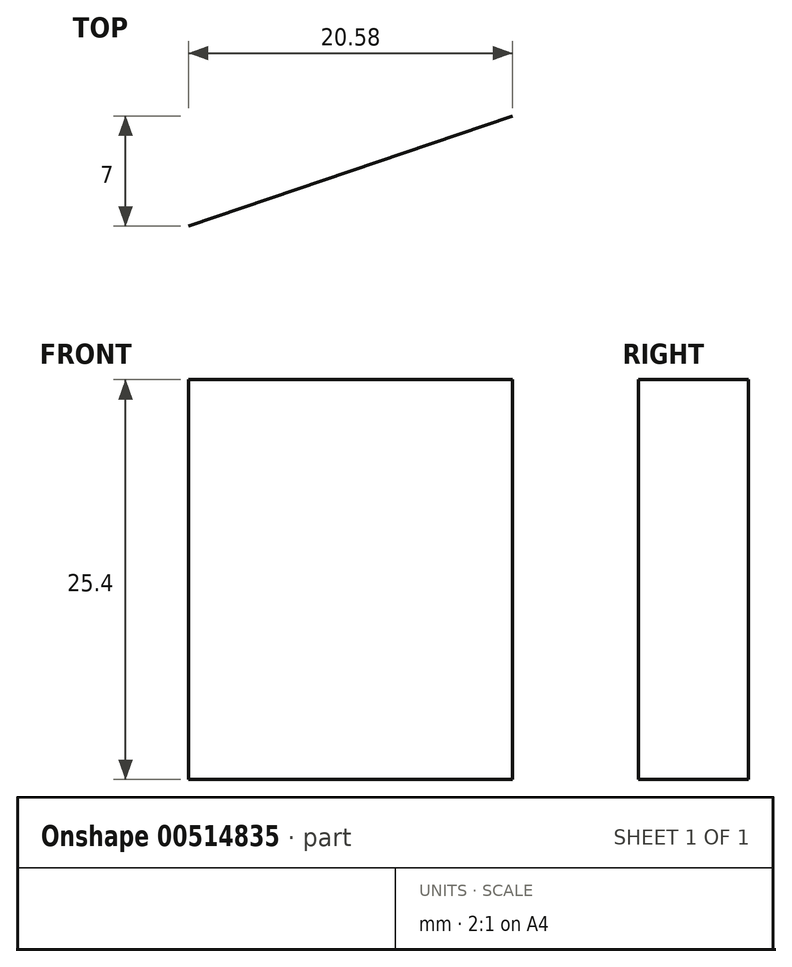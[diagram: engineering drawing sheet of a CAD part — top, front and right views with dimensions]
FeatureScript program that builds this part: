
annotation { "Feature Type Name" : "Feature", "Feature Type Description" : "" }
export const myFeature = defineFeature(function(context is Context, id is Id, definition is map)
    precondition{}
    {
        {
            var Q0;
            Q0=qCreatedBy(makeId("Top.planeOp"),FACE);
            var sketch = newSketch(context, id + "F0", { "sketchPlane" : qUnion([Q0])});
            skLineSegment(sketch, "E0", {"start": v(-65.46, 14.2) * mm, "end": v(-54.22, -25) * mm});
            skLineSegment(sketch, "E1", {"start": v(-54.22, -25) * mm, "end": v(-16.1, -37.4) * mm});
            skLineSegment(sketch, "E2", {"start": v(-16.1, -37.4) * mm, "end": v(6.83, -40.7) * mm});
            skLineSegment(sketch, "E3", {"start": v(6.83, -40.7) * mm, "end": v(27.4, -33.7) * mm});
            skSolve(sketch);
        }
        {
            var Q0;
            Q0=sQuery(id+"F0.wireOp",EDGE,"E3");
            extrude(context, id + "F1", {"bodyType" : ToolBodyType.SURFACE, "surfaceEntities" : qUnion([Q0]), "depth" : 25.4 * mm, "offsetDistance" : 25.4 * mm});
        }
    });
